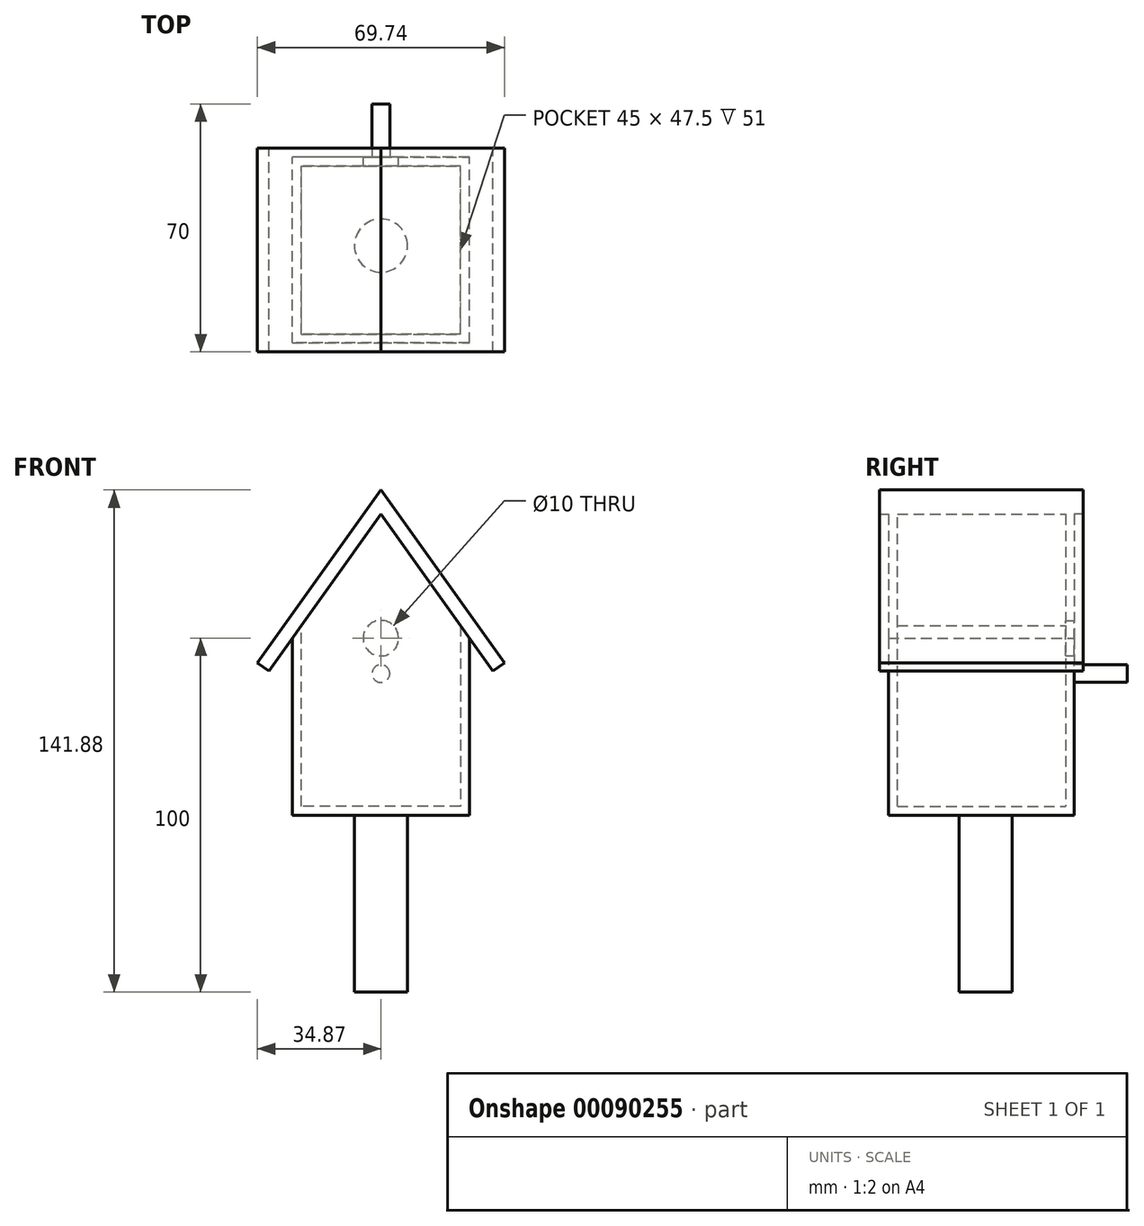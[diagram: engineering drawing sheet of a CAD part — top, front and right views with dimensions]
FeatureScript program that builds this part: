
annotation { "Feature Type Name" : "Feature", "Feature Type Description" : "" }
export const myFeature = defineFeature(function(context is Context, id is Id, definition is map)
    precondition{}
    {
        {
            var Q0;
            Q0=qCreatedBy(makeId("Front.planeOp"),FACE);
            var sketch = newSketch(context, id + "F0", { "sketchPlane" : qUnion([Q0])});
            skLineSegment(sketch, "E0.bottom", {"start": v(25, 25) * mm, "end": v(-25, 25) * mm, "construction": true});
            skLineSegment(sketch, "E0.top", {"start": v(25, -25) * mm, "end": v(-25, -25) * mm});
            skLineSegment(sketch, "E0.left", {"start": v(25, 25) * mm, "end": v(25, -25) * mm});
            skLineSegment(sketch, "E0.right", {"start": v(-25, 25) * mm, "end": v(-25, -25) * mm});
            skPoint(sketch, "E0.middle", {"position": v(0, 0) * mm});
            skLineSegment(sketch, "E1", {"start": v(-25, 25) * mm, "end": v(0, 60) * mm});
            skLineSegment(sketch, "E2", {"start": v(0, 60) * mm, "end": v(25, 25) * mm});
            skLineSegment(sketch, "E3", {"start": v(25, 25) * mm, "end": v(31.62, 15.73) * mm});
            skLineSegment(sketch, "E4", {"start": v(31.62, 15.73) * mm, "end": v(34.87, 18.06) * mm});
            skLineSegment(sketch, "E5", {"start": v(34.87, 18.06) * mm, "end": v(0, 66.88) * mm});
            skLineSegment(sketch, "E6.MirrorCS", {"start": v(-34.87, 18.06) * mm, "end": v(0, 66.88) * mm});
            skLineSegment(sketch, "E7.MirrorCS", {"start": v(-31.62, 15.73) * mm, "end": v(-34.87, 18.06) * mm});
            skLineSegment(sketch, "E8.MirrorCS", {"start": v(-25, 25) * mm, "end": v(-31.62, 15.73) * mm});
            skCircle(sketch, "E9", {"center": v(0, 25) * mm, "radius": 5 * mm});
            skCircle(sketch, "E10", {"center": v(0, 15) * mm, "radius": 2.5 * mm});
            skLineSegment(sketch, "E11.0", {"start": v(22.5, 25) * mm, "end": v(22.5, -22.5) * mm});
            skLineSegment(sketch, "E11.1", {"start": v(22.5, -22.5) * mm, "end": v(-22.5, -22.5) * mm});
            skLineSegment(sketch, "E11.2", {"start": v(-22.5, 25) * mm, "end": v(-22.5, -22.5) * mm});
            skLineSegment(sketch, "E12", {"start": v(-22.5, 25) * mm, "end": v(-22.5, 28.5) * mm});
            skLineSegment(sketch, "E13", {"start": v(22.5, 25) * mm, "end": v(22.5, 28.5) * mm});
            skSolve(sketch);
        }
        {
            var Q0;
            Q0=makeQuery(id+"F0.imprint","IMPRINT",FACE,{"disambiguationData":[TD([[makeQuery(id+"F0.imprint","IMPRINT",EDGE,{"derivedFrom":sQuery(id+"F0.wireOp",EDGE,"E9")}),-1.0]])]});
            var Q1;
            Q1=makeQuery(id+"F0.imprint","IMPRINT",FACE,{"disambiguationData":[TD([[makeQuery(id+"F0.imprint","IMPRINT",EDGE,{"derivedFrom":sQuery(id+"F0.wireOp",EDGE,"E10")}),1.0]])]});
            extrude(context, id + "F1", {"entities" : qUnion([Q0, Q1]), "depth" : 2.5 * mm});
        }
        {
            var Q0;
            Q0=makeQuery(id+"F0.imprint","IMPRINT",FACE,{"disambiguationData":[TD([[makeQuery(id+"F0.imprint","IMPRINT",EDGE,{"derivedFrom":sQuery(id+"F0.wireOp",EDGE,"E0.top")}),-1.0]])]});
            extrude(context, id + "F2", {"entities" : qUnion([Q0]), "operationType" : NewBodyOperationType.ADD, "depth" : 50 * mm});
        }
        {
            var Q0;
            Q0=makeQuery(id+"F2.opExtrude","CAP_FACE",FACE,{"disambiguationData":[OSD([sQuery(id+"F0.wireOp",EDGE,"E0.top"),sQuery(id+"F0.wireOp",EDGE,"E0.left"),sQuery(id+"F0.wireOp",EDGE,"E0.right"),sQuery(id+"F0.wireOp",EDGE,"E1"),sQuery(id+"F0.wireOp",EDGE,"E2"),sQuery(id+"F0.wireOp",EDGE,"E11.0"),sQuery(id+"F0.wireOp",EDGE,"E11.1"),sQuery(id+"F0.wireOp",EDGE,"E11.2"),sQuery(id+"F0.wireOp",EDGE,"E12"),sQuery(id+"F0.wireOp",EDGE,"E13")])],"isStart":false});
            var sketch = newSketch(context, id + "F3", { "sketchPlane" : qUnion([Q0])});
            skLineSegment(sketch, "E14.0", {"start": v(22.5, 25) * mm, "end": v(22.5, 28.5) * mm});
            skLineSegment(sketch, "E15.0", {"start": v(-22.5, 25) * mm, "end": v(-22.5, 28.5) * mm});
            skLineSegment(sketch, "E16.0", {"start": v(-22.5, 25) * mm, "end": v(-22.5, -22.5) * mm});
            skLineSegment(sketch, "E17.0", {"start": v(22.5, -22.5) * mm, "end": v(-22.5, -22.5) * mm});
            skLineSegment(sketch, "E18.0", {"start": v(22.5, 25) * mm, "end": v(22.5, -22.5) * mm});
            skLineSegment(sketch, "E19.0", {"start": v(25, 25) * mm, "end": v(25, -25) * mm});
            skLineSegment(sketch, "E20.0", {"start": v(25, -25) * mm, "end": v(-25, -25) * mm});
            skLineSegment(sketch, "E21.0", {"start": v(-25, 25) * mm, "end": v(-25, -25) * mm});
            skLineSegment(sketch, "E22.0", {"start": v(-25, 25) * mm, "end": v(0, 60) * mm});
            skLineSegment(sketch, "E23.0", {"start": v(0, 60) * mm, "end": v(25, 25) * mm});
            skSolve(sketch);
        }
        {
            var Q0;
            {var subQ3=sQuery(id+"F3.wireOp",EDGE,"E14.0");Q0=makeQuery(id+"F3.imprint","IMPRINT",FACE,{"disambiguationData":[TD([[makeQuery(id+"F3.imprint","IMPRINT",EDGE,{"derivedFrom":subQ3}),-1.0]])]});}
            var Q1;
            {var subQ1=sQuery(id+"F3.wireOp",EDGE,"E14.0");Q1=makeQuery(id+"F3.imprint","IMPRINT",FACE,{"disambiguationData":[TD([[makeQuery(id+"F3.imprint","IMPRINT",EDGE,{"derivedFrom":subQ1}),1.0]])]});}
            extrude(context, id + "F4", {"entities" : qUnion([Q0, Q1]), "operationType" : NewBodyOperationType.ADD, "depth" : 2.5 * mm});
        }
        {
            var Q0;
            {var subQ0=sQuery(id+"F0.wireOp",EDGE,"E3");Q0=makeQuery(id+"F0.imprint","IMPRINT",FACE,{"disambiguationData":[TD([[makeQuery(id+"F0.imprint","IMPRINT",EDGE,{"derivedFrom":subQ0}),1.0]])]});}
            extrude(context, id + "F5", {"entities" : qUnion([Q0]), "operationType" : NewBodyOperationType.ADD, "depth" : 55 * mm});
        }
        {
            var Q0;
            {var subQ0=sQuery(id+"F0.wireOp",EDGE,"E3");Q0=makeQuery(id+"F0.imprint","IMPRINT",FACE,{"disambiguationData":[TD([[makeQuery(id+"F0.imprint","IMPRINT",EDGE,{"derivedFrom":subQ0}),1.0]])]});}
            extrude(context, id + "F6", {"entities" : qUnion([Q0]), "operationType" : NewBodyOperationType.ADD, "oppositeDirection" : true, "depth" : 2.5 * mm});
        }
        {
            var Q0;
            Q0=makeQuery(id+"F0.imprint","IMPRINT",FACE,{"disambiguationData":[TD([[makeQuery(id+"F0.imprint","IMPRINT",EDGE,{"derivedFrom":sQuery(id+"F0.wireOp",EDGE,"E10")}),1.0]])]});
            extrude(context, id + "F7", {"entities" : qUnion([Q0]), "operationType" : NewBodyOperationType.ADD, "oppositeDirection" : true, "depth" : 15 * mm});
        }
        {
            var Q0;
            Q0=makeQuery(id+"F4.boolean.opBoolean","MERGE",FACE,{"derivedFrom":[makeQuery(id+"F2.opExtrude","SWEPT_FACE",FACE,{"disambiguationData":[OSD([sQuery(id+"F0.wireOp",EDGE,"E0.top")])]}),makeQuery(id+"F4.opExtrude","SWEPT_FACE",FACE,{"disambiguationData":[OSD([sQuery(id+"F3.wireOp",EDGE,"E20.0")])]})]});
            var sketch = newSketch(context, id + "F8", { "sketchPlane" : qUnion([Q0])});
            skCircle(sketch, "E24", {"center": v(0, 25) * mm, "radius": 7.5 * mm});
            skSolve(sketch);
        }
        {
            var Q0;
            Q0=makeQuery(id+"F8.imprint","IMPRINT",FACE,{"disambiguationData":[TD([[makeQuery(id+"F8.imprint","IMPRINT",EDGE,{"derivedFrom":sQuery(id+"F8.wireOp",EDGE,"E24")}),1.0]])]});
            extrude(context, id + "F9", {"entities" : qUnion([Q0]), "operationType" : NewBodyOperationType.ADD, "depth" : 50 * mm});
        }
    });
